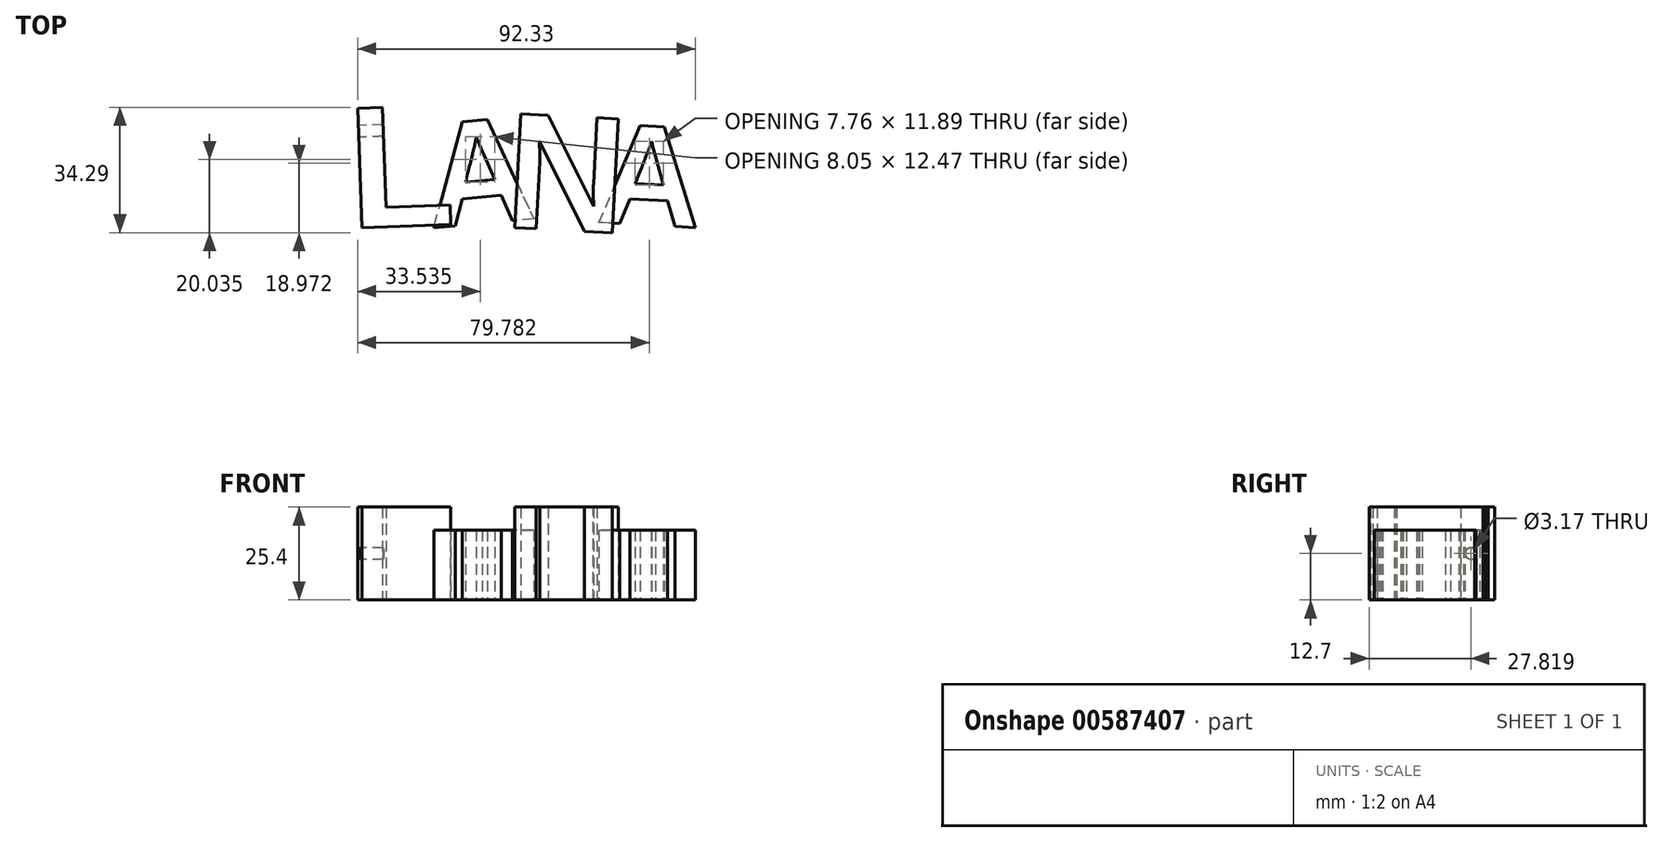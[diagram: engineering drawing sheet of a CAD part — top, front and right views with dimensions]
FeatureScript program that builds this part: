
annotation { "Feature Type Name" : "Feature", "Feature Type Description" : "" }
export const myFeature = defineFeature(function(context is Context, id is Id, definition is map)
    precondition{}
    {
        {
            var Q0;
            Q0=qCreatedBy(makeId("Top.planeOp"),FACE);
            var sketch = newSketch(context, id + "F0", { "sketchPlane" : qUnion([Q0])});
            skText(sketch, "E0", { "text": "L", "fontName": "Arimo-Bold.ttf"});
            const initialGuessF0  = {"E0": [-0.01542, 0, 1, 0, 0.0342]};
            skSetInitialGuess(sketch, initialGuessF0);
            skSolve(sketch);
        }
        {
            var Q0;
            Q0=qCreatedBy(makeId("Top.planeOp"),FACE);
            var sketch = newSketch(context, id + "F1", { "sketchPlane" : qUnion([Q0])});
            skText(sketch, "E1", { "text": "A", "fontName": "Arimo-Bold.ttf"});
            const initialGuessF1  = {"E1": [0.00647, 0, 1, 0, 0.02941]};
            skSetInitialGuess(sketch, initialGuessF1);
            skSolve(sketch);
        }
        {
            var Q0;
            Q0=qCreatedBy(makeId("Top.planeOp"),FACE);
            var sketch = newSketch(context, id + "F2", { "sketchPlane" : qUnion([Q0])});
            skText(sketch, "E2", { "text": "N", "fontName": "Arimo-Bold.ttf"});
            const initialGuessF2  = {"E2": [0.03551, 0, 1, 0, 0.0326]};
            skSetInitialGuess(sketch, initialGuessF2);
            skSolve(sketch);
        }
        {
            var Q0;
            Q0=qCreatedBy(makeId("Top.planeOp"),FACE);
            var sketch = newSketch(context, id + "F3", { "sketchPlane" : qUnion([Q0])});
            skText(sketch, "E3", { "text": "A", "fontName": "Arimo-Bold.ttf"});
            const initialGuessF3  = {"E3": [0.06736, 0, 1, 0, 0.02829]};
            skSetInitialGuess(sketch, initialGuessF3);
            skSolve(sketch);
        }
        {
            var Q0;
            Q0 = qSketchRegion(id + "F0", true);
            extrude(context, id + "F4", {"entities" : qUnion([Q0]), "depth" : 25.4 * mm, "offsetDistance" : 25.4 * mm});
        }
        {
            var Q0;
            Q0=makeQuery(id+"F1.imprint","IMPRINT",FACE,{"disambiguationData":[TD([[makeQuery(id+"F1.imprint","IMPRINT",EDGE,{"derivedFrom":sQuery(id+"F1.wireOp",EDGE,"E1.sketch_text.stroke-0")}),-1.0]])]});
            extrude(context, id + "F5", {"entities" : qUnion([Q0]), "depth" : 19.05 * mm, "offsetDistance" : 25.4 * mm});
        }
        {
            var Q0;
            Q0=makeQuery(id+"F2.imprint","IMPRINT",FACE,{"disambiguationData":[TD([[makeQuery(id+"F2.imprint","IMPRINT",EDGE,{"derivedFrom":sQuery(id+"F2.wireOp",EDGE,"E2.sketch_text.stroke-0")}),-1.0]])]});
            extrude(context, id + "F6", {"entities" : qUnion([Q0]), "depth" : 25.4 * mm, "offsetDistance" : 25.4 * mm});
        }
        {
            var Q0;
            Q0=makeQuery(id+"F3.imprint","IMPRINT",FACE,{"disambiguationData":[TD([[makeQuery(id+"F3.imprint","IMPRINT",EDGE,{"derivedFrom":sQuery(id+"F3.wireOp",EDGE,"E3.sketch_text.stroke-0")}),-1.0]])]});
            extrude(context, id + "F7", {"entities" : qUnion([Q0]), "depth" : 19.05 * mm, "offsetDistance" : 25.4 * mm});
        }
        {
            var Q0;
            Q0=makeQuery(id+"F5.opExtrude","SWEPT_BODY",BODY,{"disambiguationData":[OSD([sQuery(id+"F1.wireOp",EDGE,"E1.sketch_text.stroke-0"),sQuery(id+"F1.wireOp",EDGE,"E1.sketch_text.stroke-1"),sQuery(id+"F1.wireOp",EDGE,"E1.sketch_text.stroke-2"),sQuery(id+"F1.wireOp",EDGE,"E1.sketch_text.stroke-3"),sQuery(id+"F1.wireOp",EDGE,"E1.sketch_text.stroke-4"),sQuery(id+"F1.wireOp",EDGE,"E1.sketch_text.stroke-5"),sQuery(id+"F1.wireOp",EDGE,"E1.sketch_text.stroke-6"),sQuery(id+"F1.wireOp",EDGE,"E1.sketch_text.stroke-7"),sQuery(id+"F1.wireOp",EDGE,"E1.sketch_text.stroke-8"),sQuery(id+"F1.wireOp",EDGE,"E1.sketch_text.stroke-9"),sQuery(id+"F1.wireOp",EDGE,"E1.sketch_text.stroke-10"),sQuery(id+"F1.wireOp",EDGE,"E1.sketch_text.stroke-11"),sQuery(id+"F1.wireOp",EDGE,"E1.sketch_text.stroke-12"),sQuery(id+"F1.wireOp",EDGE,"E1.sketch_text.stroke-13"),sQuery(id+"F1.wireOp",EDGE,"E1.sketch_text.stroke-14")])]});
            var Q1;
            Q1=makeQuery(id+"F5.opExtrude","SWEPT_EDGE",EDGE,{"disambiguationData":[OSD([sQuery(id+"F1.wireOp",EDGE,"E1.sketch_text.stroke-3"),sQuery(id+"F1.wireOp",EDGE,"E1.sketch_text.stroke-4")])]});
            transform(context, id + "F8", {"entities" : qUnion([Q0]), "transformType" : TransformType.ROTATION, "transformAxis" : qUnion([Q1]), "angle" : 5 * degree, "oppositeDirection" : true, "makeCopy" : false});
        }
        {
            var Q0;
            Q0=makeQuery(id+"F6.opExtrude","SWEPT_BODY",BODY,{"disambiguationData":[OSD([sQuery(id+"F2.wireOp",EDGE,"E2.sketch_text.stroke-0"),sQuery(id+"F2.wireOp",EDGE,"E2.sketch_text.stroke-1"),sQuery(id+"F2.wireOp",EDGE,"E2.sketch_text.stroke-2"),sQuery(id+"F2.wireOp",EDGE,"E2.sketch_text.stroke-3"),sQuery(id+"F2.wireOp",EDGE,"E2.sketch_text.stroke-4"),sQuery(id+"F2.wireOp",EDGE,"E2.sketch_text.stroke-5"),sQuery(id+"F2.wireOp",EDGE,"E2.sketch_text.stroke-6"),sQuery(id+"F2.wireOp",EDGE,"E2.sketch_text.stroke-7"),sQuery(id+"F2.wireOp",EDGE,"E2.sketch_text.stroke-8"),sQuery(id+"F2.wireOp",EDGE,"E2.sketch_text.stroke-9"),sQuery(id+"F2.wireOp",EDGE,"E2.sketch_text.stroke-10"),sQuery(id+"F2.wireOp",EDGE,"E2.sketch_text.stroke-11")])]});
            transform(context, id + "F9", {"entities" : qUnion([Q0]), "transformType" : TransformType.TRANSLATION_3D, "dx" : -8.9 * mm, "dy" : 0 * mm, "dz" : 0 * mm, "makeCopy" : false});
        }
        {
            var Q0;
            Q0=makeQuery(id+"F6.opExtrude","SWEPT_BODY",BODY,{"disambiguationData":[OSD([sQuery(id+"F2.wireOp",EDGE,"E2.sketch_text.stroke-0"),sQuery(id+"F2.wireOp",EDGE,"E2.sketch_text.stroke-1"),sQuery(id+"F2.wireOp",EDGE,"E2.sketch_text.stroke-2"),sQuery(id+"F2.wireOp",EDGE,"E2.sketch_text.stroke-3"),sQuery(id+"F2.wireOp",EDGE,"E2.sketch_text.stroke-4"),sQuery(id+"F2.wireOp",EDGE,"E2.sketch_text.stroke-5"),sQuery(id+"F2.wireOp",EDGE,"E2.sketch_text.stroke-6"),sQuery(id+"F2.wireOp",EDGE,"E2.sketch_text.stroke-7"),sQuery(id+"F2.wireOp",EDGE,"E2.sketch_text.stroke-8"),sQuery(id+"F2.wireOp",EDGE,"E2.sketch_text.stroke-9"),sQuery(id+"F2.wireOp",EDGE,"E2.sketch_text.stroke-10"),sQuery(id+"F2.wireOp",EDGE,"E2.sketch_text.stroke-11")])]});
            var Q1;
            Q1=makeQuery(id+"F6.opExtrude","SWEPT_EDGE",EDGE,{"disambiguationData":[OSD([sQuery(id+"F2.wireOp",EDGE,"E2.sketch_text.stroke-3"),sQuery(id+"F2.wireOp",EDGE,"E2.sketch_text.stroke-4")])]});
            transform(context, id + "F10", {"entities" : qUnion([Q0]), "transformType" : TransformType.ROTATION, "transformAxis" : qUnion([Q1]), "angle" : 3 * degree, "makeCopy" : false});
        }
        {
            var Q0;
            Q0=makeQuery(id+"F7.opExtrude","SWEPT_BODY",BODY,{"disambiguationData":[OSD([sQuery(id+"F3.wireOp",EDGE,"E3.sketch_text.stroke-0"),sQuery(id+"F3.wireOp",EDGE,"E3.sketch_text.stroke-1"),sQuery(id+"F3.wireOp",EDGE,"E3.sketch_text.stroke-2"),sQuery(id+"F3.wireOp",EDGE,"E3.sketch_text.stroke-3"),sQuery(id+"F3.wireOp",EDGE,"E3.sketch_text.stroke-4"),sQuery(id+"F3.wireOp",EDGE,"E3.sketch_text.stroke-5"),sQuery(id+"F3.wireOp",EDGE,"E3.sketch_text.stroke-6"),sQuery(id+"F3.wireOp",EDGE,"E3.sketch_text.stroke-7"),sQuery(id+"F3.wireOp",EDGE,"E3.sketch_text.stroke-8"),sQuery(id+"F3.wireOp",EDGE,"E3.sketch_text.stroke-9"),sQuery(id+"F3.wireOp",EDGE,"E3.sketch_text.stroke-10"),sQuery(id+"F3.wireOp",EDGE,"E3.sketch_text.stroke-11"),sQuery(id+"F3.wireOp",EDGE,"E3.sketch_text.stroke-12"),sQuery(id+"F3.wireOp",EDGE,"E3.sketch_text.stroke-13"),sQuery(id+"F3.wireOp",EDGE,"E3.sketch_text.stroke-14")])]});
            transform(context, id + "F11", {"entities" : qUnion([Q0]), "transformType" : TransformType.TRANSLATION_3D, "dx" : -15.75 * mm, "dy" : 0 * mm, "dz" : 0 * mm, "makeCopy" : false});
        }
        {
            var Q0;
            Q0=makeQuery(id+"F7.opExtrude","SWEPT_BODY",BODY,{"disambiguationData":[OSD([sQuery(id+"F3.wireOp",EDGE,"E3.sketch_text.stroke-0"),sQuery(id+"F3.wireOp",EDGE,"E3.sketch_text.stroke-1"),sQuery(id+"F3.wireOp",EDGE,"E3.sketch_text.stroke-2"),sQuery(id+"F3.wireOp",EDGE,"E3.sketch_text.stroke-3"),sQuery(id+"F3.wireOp",EDGE,"E3.sketch_text.stroke-4"),sQuery(id+"F3.wireOp",EDGE,"E3.sketch_text.stroke-5"),sQuery(id+"F3.wireOp",EDGE,"E3.sketch_text.stroke-6"),sQuery(id+"F3.wireOp",EDGE,"E3.sketch_text.stroke-7"),sQuery(id+"F3.wireOp",EDGE,"E3.sketch_text.stroke-8"),sQuery(id+"F3.wireOp",EDGE,"E3.sketch_text.stroke-9"),sQuery(id+"F3.wireOp",EDGE,"E3.sketch_text.stroke-10"),sQuery(id+"F3.wireOp",EDGE,"E3.sketch_text.stroke-11"),sQuery(id+"F3.wireOp",EDGE,"E3.sketch_text.stroke-12"),sQuery(id+"F3.wireOp",EDGE,"E3.sketch_text.stroke-13"),sQuery(id+"F3.wireOp",EDGE,"E3.sketch_text.stroke-14")])]});
            var Q1;
            Q1=makeQuery(id+"F7.opExtrude","SWEPT_EDGE",EDGE,{"disambiguationData":[OSD([sQuery(id+"F3.wireOp",EDGE,"E3.sketch_text.stroke-6"),sQuery(id+"F3.wireOp",EDGE,"E3.sketch_text.stroke-7")])]});
            transform(context, id + "F12", {"entities" : qUnion([Q0]), "transformType" : TransformType.ROTATION, "transformAxis" : qUnion([Q1]), "angle" : 3 * degree, "makeCopy" : false});
        }
        {
            var Q0;
            Q0=makeQuery(id+"F4.opExtrude","SWEPT_BODY",BODY,{"disambiguationData":[OSD([sQuery(id+"F0.wireOp",EDGE,"E0.sketch_text.stroke-0"),sQuery(id+"F0.wireOp",EDGE,"E0.sketch_text.stroke-1"),sQuery(id+"F0.wireOp",EDGE,"E0.sketch_text.stroke-2"),sQuery(id+"F0.wireOp",EDGE,"E0.sketch_text.stroke-3"),sQuery(id+"F0.wireOp",EDGE,"E0.sketch_text.stroke-4"),sQuery(id+"F0.wireOp",EDGE,"E0.sketch_text.stroke-5")])]});
            var Q1;
            Q1=makeQuery(id+"F4.opExtrude","SWEPT_EDGE",EDGE,{"disambiguationData":[OSD([sQuery(id+"F0.wireOp",EDGE,"E0.sketch_text.stroke-0"),sQuery(id+"F0.wireOp",EDGE,"E0.sketch_text.stroke-5")])]});
            transform(context, id + "F13", {"entities" : qUnion([Q0]), "transformType" : TransformType.ROTATION, "transformAxis" : qUnion([Q1]), "angle" : 2 * degree, "oppositeDirection" : true, "makeCopy" : false});
        }
        {
            var Q0;
            Q0=makeQuery(id+"F4.opExtrude","SWEPT_FACE",FACE,{"disambiguationData":[OSD([sQuery(id+"F0.wireOp",EDGE,"E0.sketch_text.stroke-0")])]});
            var sketch = newSketch(context, id + "F14", { "sketchPlane" : qUnion([Q0])});
            skCircle(sketch, "E4", {"center": v(-26.75, 12.7) * mm, "radius": 1.59 * mm});
            skPoint(sketch, "E4.centerSnap0", {"position": v(-33.1, 12.7) * mm});
            skSolve(sketch);
        }
        {
            var Q0;
            Q0 = qSketchRegion(id + "F14", true);
            extrude(context, id + "F15", {"entities" : qUnion([Q0]), "operationType" : NewBodyOperationType.REMOVE, "endBound" : BoundingType.UP_TO_NEXT, "oppositeDirection" : true, "depth" : 25.4 * mm, "offsetDistance" : 25.4 * mm});
        }
    });
